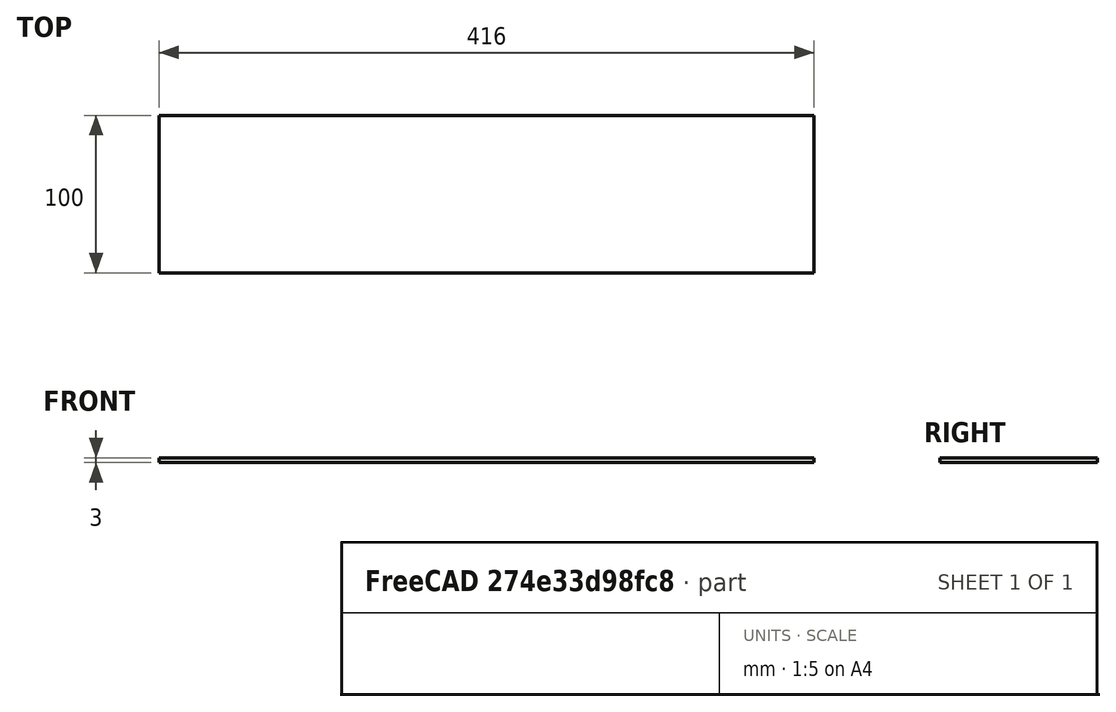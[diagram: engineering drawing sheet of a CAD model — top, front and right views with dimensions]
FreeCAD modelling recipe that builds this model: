
FCSTD DOCUMENT  (FreeCAD 1.0R39319 (Git))
Label: 12_lamella_sheet_no_knob
License: All rights reserved
LicenseURL: http://en.wikipedia.org/wiki/All_rights_reserved
objects: Spreadsheet::Sheet×1, Sketcher::SketchObject×1, PartDesign::Pad×1, PartDesign::Body×1
note: 6 computed .brp shape members not serialized (recipe doc carries the construction recipe); baked Part::Feature solids carry a one-line shape summary decoded from their .brp

FEATURE [Spreadsheet::Sheet] Spreadsheet
  cells = A4='length; B4(length)=416; A5='width; B5(width)=100; A6='height; B6(height)=3
FEATURE [Sketcher::SketchObject] Sketch
  ArcFitTolerance = 1e-06
  AttachmentSupport = -> [XY_Plane]
  FullyConstrained = true
  MakeInternals = false
  MapMode = 5
  expr: Constraints[11] = Spreadsheet.length
  expr: Constraints[12] = Spreadsheet.width
  sketch-geometry (5):
    g0: LineSegment StartX=-208 StartY=50 StartZ=0 EndX=-208 EndY=-50 EndZ=0
    g1: LineSegment StartX=-208 StartY=-50 StartZ=0 EndX=208 EndY=-50 EndZ=0
    g2: LineSegment StartX=208 StartY=-50 StartZ=0 EndX=208 EndY=50 EndZ=0
    g3: LineSegment StartX=208 StartY=50 StartZ=0 EndX=-208 EndY=50 EndZ=0
    g4: LineSegment [constr] StartX=-208 StartY=50 StartZ=0 EndX=208 EndY=-50 EndZ=0
  constraints (13):
    c: Coincident(g0,g1)
    c: Coincident(g1,g2)
    c: Coincident(g2,g3)
    c: Coincident(g3,g0)
    c: Vertical(g0)
    c: Vertical(g2)
    c: Horizontal(g1)
    c: Horizontal(g3)
    c: Coincident(g4,g0)
    c: Coincident(g4,g1)
    c: Symmetric(g4,g4,g-1)
    c: DistanceX(g3,g3) = 416
    c: DistanceY(g0,g0) = 100
FEATURE [PartDesign::Pad] Pad
  Direction = (0,0,1)
  Length = 3
  Length2 = 10
  Midplane = true
  Profile = -> Sketch
  ReferenceAxis = -> Sketch [N_Axis]
  Suppressed = false
  Type = 0
  expr: Length = Spreadsheet.height
FEATURE [PartDesign::Body] Body
  AllowCompound = false
  Group = -> [Sketch,Pad]
  Origin = -> Origin
  Tip = -> Pad
